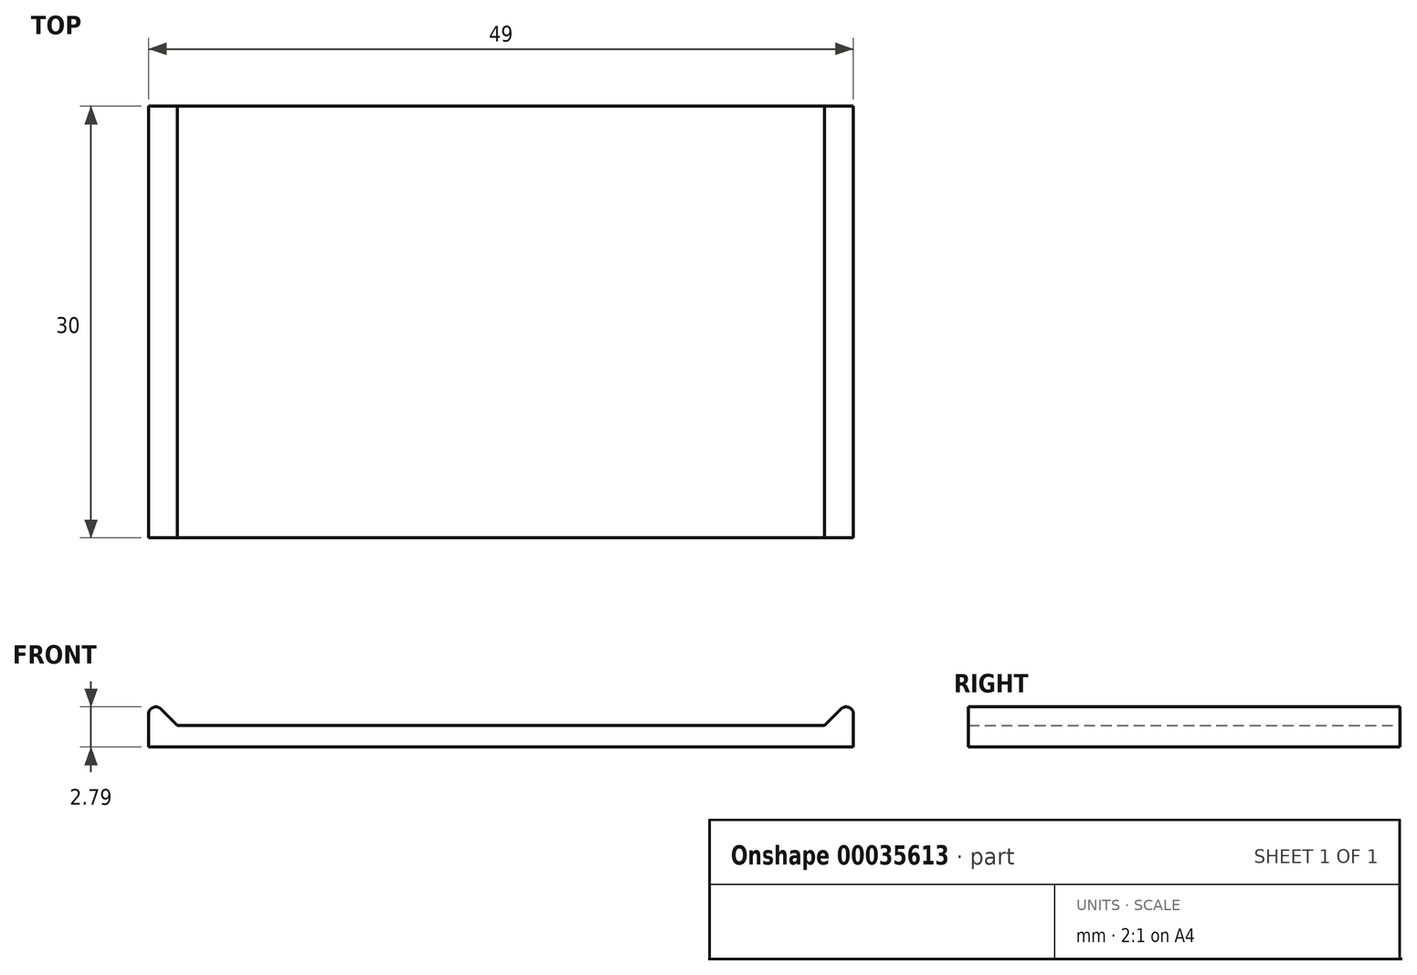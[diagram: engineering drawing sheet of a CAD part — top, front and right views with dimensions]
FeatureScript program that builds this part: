
annotation { "Feature Type Name" : "Feature", "Feature Type Description" : "" }
export const myFeature = defineFeature(function(context is Context, id is Id, definition is map)
    precondition{}
    {
        {
            var Q0;
            Q0=qCreatedBy(makeId("Front.planeOp"),FACE);
            var sketch = newSketch(context, id + "F0", { "sketchPlane" : qUnion([Q0])});
            skLineSegment(sketch, "E0.bottom", {"start": v(-24.5, 0) * mm, "end": v(24.5, 0) * mm});
            skLineSegment(sketch, "E0.top", {"start": v(-24.5, 1.5) * mm, "end": v(24.5, 1.5) * mm});
            skLineSegment(sketch, "E0.left", {"start": v(-24.5, 0) * mm, "end": v(-24.5, 1.5) * mm});
            skLineSegment(sketch, "E0.right", {"start": v(24.5, 0) * mm, "end": v(24.5, 1.5) * mm});
            skLineSegment(sketch, "E1", {"start": v(-24.5, 1.5) * mm, "end": v(-24.5, 3.5) * mm});
            skLineSegment(sketch, "E2", {"start": v(-24.5, 3.5) * mm, "end": v(-22.5, 1.5) * mm});
            skLineSegment(sketch, "E3", {"start": v(24.5, 1.5) * mm, "end": v(24.5, 3.5) * mm});
            skLineSegment(sketch, "E4", {"start": v(24.5, 3.5) * mm, "end": v(22.5, 1.5) * mm});
            skSolve(sketch);
        }
        {
            var Q0;
            Q0 = qSketchRegion(id + "F0", true);
            extrude(context, id + "F1", {"entities" : qUnion([Q0]), "depth" : 30 * mm, "symmetric" : true});
        }
        {
            var Q0;
            Q0=makeQuery(id+"F1.opExtrude","SWEPT_EDGE",EDGE,{"disambiguationData":[OSD([sQuery(id+"F0.wireOp",EDGE,"E1"),sQuery(id+"F0.wireOp",EDGE,"E2")])]});
            var Q1;
            Q1=makeQuery(id+"F1.opExtrude","SWEPT_EDGE",EDGE,{"disambiguationData":[OSD([sQuery(id+"F0.wireOp",EDGE,"E3"),sQuery(id+"F0.wireOp",EDGE,"E4")])]});
            fillet(context, id + "F2", {"entities" : qUnion([Q0, Q1]), "radius" : .5 * mm, "tangentPropagation" : true, "allowEdgeOverflow" : false});
        }
    });
